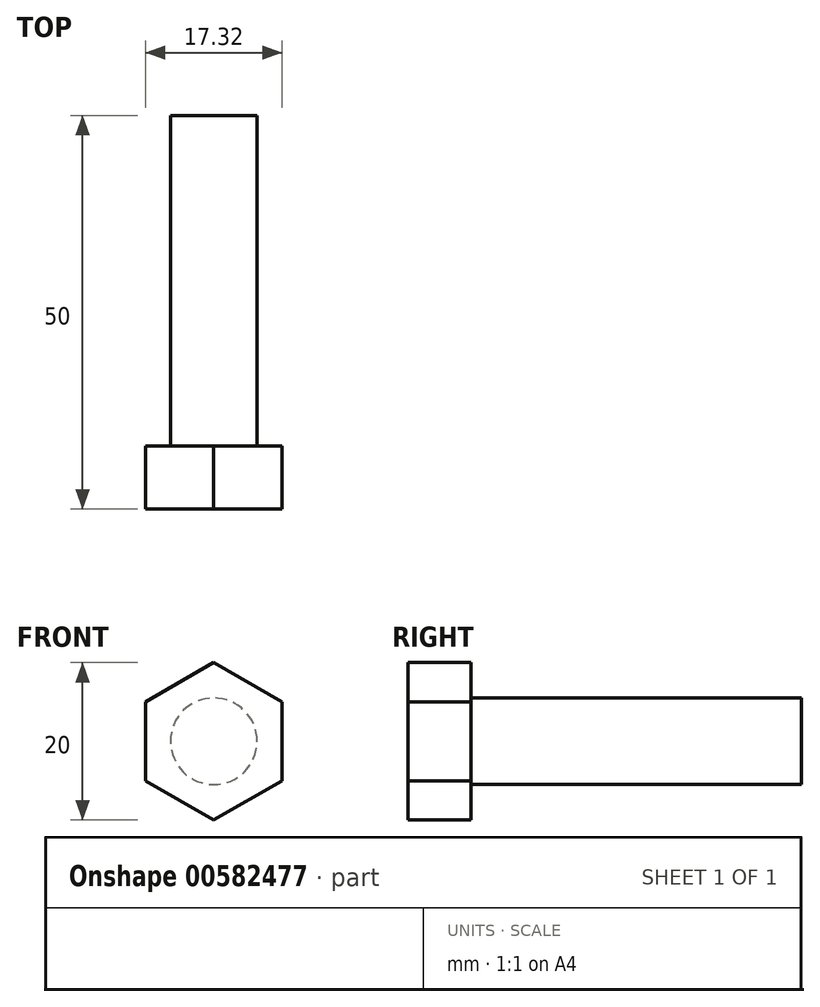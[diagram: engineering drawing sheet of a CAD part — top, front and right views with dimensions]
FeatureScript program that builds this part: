
annotation { "Feature Type Name" : "Feature", "Feature Type Description" : "" }
export const myFeature = defineFeature(function(context is Context, id is Id, definition is map)
    precondition{}
    {
        {
            var Q0;
            Q0=qCreatedBy(makeId("Front.planeOp"),FACE);
            var sketch = newSketch(context, id + "F0", { "sketchPlane" : qUnion([Q0])});
            skCircle(sketch, "E0", {"center": v(0, 0) * mm, "radius": 5.5 * mm});
            skCircle(sketch, "E1.cCircle", {"center": v(0, 0) * mm, "radius": 10 * mm, "construction": true});
            skLineSegment(sketch, "E1.0", {"start": v(0, 10) * mm, "end": v(8.66, 5) * mm});
            skLineSegment(sketch, "E1.1", {"start": v(8.66, 5) * mm, "end": v(8.66, -5) * mm});
            skLineSegment(sketch, "E1.2", {"start": v(8.66, -5) * mm, "end": v(0, -10) * mm});
            skLineSegment(sketch, "E1.3", {"start": v(0, -10) * mm, "end": v(-8.66, -5) * mm});
            skLineSegment(sketch, "E1.4", {"start": v(-8.66, -5) * mm, "end": v(-8.66, 5) * mm});
            skLineSegment(sketch, "E1.5", {"start": v(-8.66, 5) * mm, "end": v(0, 10) * mm});
            skSolve(sketch);
        }
        {
            var Q0;
            Q0=makeQuery(id+"F0.imprint","IMPRINT",FACE,{"disambiguationData":[TD([[makeQuery(id+"F0.imprint","IMPRINT",EDGE,{"derivedFrom":sQuery(id+"F0.wireOp",EDGE,"E0")}),-1.0]])]});
            extrude(context, id + "F1", {"entities" : qUnion([Q0]), "oppositeDirection" : true, "depth" : 8 * mm, "offsetDistance" : 25 * mm});
        }
        {
            var Q0;
            Q0=qCreatedBy(makeId("Front.planeOp"),FACE);
            var sketch = newSketch(context, id + "F2", { "sketchPlane" : qUnion([Q0])});
            skCircle(sketch, "E2", {"center": v(0, 0) * mm, "radius": 5.5 * mm});
            skSolve(sketch);
        }
        {
            var Q0;
            Q0=makeQuery(id+"F2.imprint","IMPRINT",FACE,{"disambiguationData":[TD([[makeQuery(id+"F2.imprint","IMPRINT",EDGE,{"derivedFrom":sQuery(id+"F2.wireOp",EDGE,"E2")}),1.0]])]});
            extrude(context, id + "F3", {"entities" : qUnion([Q0]), "operationType" : NewBodyOperationType.ADD, "oppositeDirection" : true, "depth" : 50 * mm, "offsetDistance" : 25 * mm});
        }
    });
